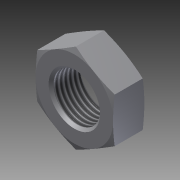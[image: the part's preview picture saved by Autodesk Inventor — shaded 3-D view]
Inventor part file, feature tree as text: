
AUTODESK INVENTOR PART (.ipt)
format: ipt  version: 2012 (Build 160160000, 160)  size: 148,992 bytes
history: native  units: in
note: dims shown in document units (in); Inventor stores cm internally (conversion verified against a paired STEP export)
features: other x70, sketch x3, revolve x2, extrude x1, thread x1
ambient origin geometry x8: Origin, YZ Plane, XZ Plane, XY Plane, X Axis, Y Axis, Z Axis, Center Point
bodies: Solid1 (feature_tree)
feature tree (77):
  sketch  "Sketch_8"  dims[d0=360.0deg d1=0.38in d2=0.0in]
  sketch  "Sketch_10"  dims[d3=360.0deg d4=0.3199in d5=0.0in]
  revolve  "Revolution1"  [1 undecoded]
  extrude  "Extrusion1"  Depth=0.3199in TaperAngle=0.0deg
  revolve  "Revolution2"  [1 undecoded]
  thread  "Thread1"  [1 undecoded]
  other  "NUT_XY"
  other  "NUT_YZ"
  other  "NUT_ZX"
  other  "NUT_X"
  other  "NUT_Y"
  other  "NUT_Z"
  other  "NUT_Center"
  other  "a1_XY"
  other  "a1_YZ"
  other  "a1_ZX"
  other  "a1_X"
  other  "a1_Y"
  other  "a1_Z"
  other  "a1_Center"
  other  "a2_XY"
  other  "a2_YZ"
  other  "a2_ZX"
  other  "a2_X"
  other  "a2_Y"
  other  "a2_Z"
  other  "a2_Center"
  other  "b1_XY"
  other  "b1_YZ"
  other  "b1_ZX"
  other  "b1_X"
  other  "b1_Y"
  other  "b1_Z"
  other  "b1_Center"
  other  "b2_XY"
  other  "b2_YZ"
  other  "b2_ZX"
  other  "b2_X"
  other  "b2_Y"
  other  "b2_Z"
  other  "b2_Center"
  other  "e_XY"
  other  "e_YZ"
  other  "e_ZX"
  other  "e_X"
  other  "e_Y"
  other  "e_Z"
  other  "e_Center"
  other  "th1_XY"
  other  "th1_YZ"
  other  "th1_ZX"
  other  "th1_X"
  other  "th1_Y"
  other  "th1_Z"
  other  "th1_Center"
  other  "th2_XY"
  other  "th2_YZ"
  other  "th2_ZX"
  other  "th2_X"
  other  "th2_Y"
  other  "th2_Z"
  other  "th2_Center"
  other  "ol1_XY"
  other  "ol1_YZ"
  other  "ol1_ZX"
  other  "ol1_X"
  other  "ol1_Y"
  other  "ol1_Z"
  other  "ol1_Center"
  other  "ol2_XY"
  other  "ol2_YZ"
  other  "ol2_ZX"
  other  "ol2_X"
  other  "ol2_Y"
  other  "ol2_Z"
  other  "ol2_Center"
  sketch  "Sketch_11"
note: 3 required parameter values undecoded (feature->parameter linkage not recoverable at this tier; creation-order binding heuristic only, values carry confidence <= 0.55)